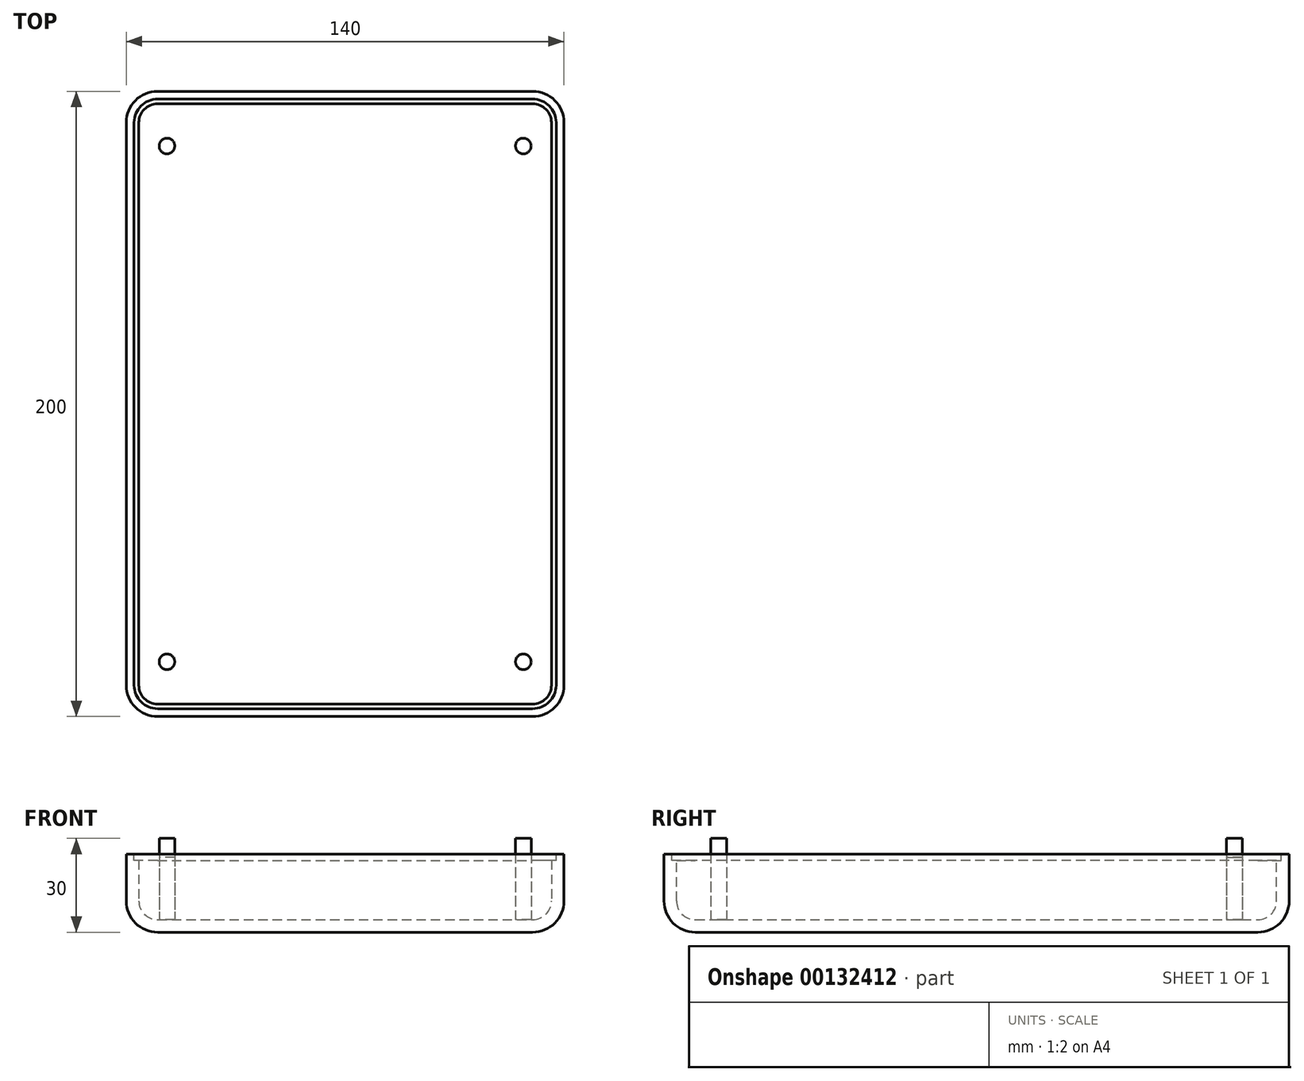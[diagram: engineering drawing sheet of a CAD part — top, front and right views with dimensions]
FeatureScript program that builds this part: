
annotation { "Feature Type Name" : "Feature", "Feature Type Description" : "" }
export const myFeature = defineFeature(function(context is Context, id is Id, definition is map)
    precondition{}
    {
        {
            var Q0;
            Q0=qCreatedBy(makeId("Top.planeOp"),FACE);
            var sketch = newSketch(context, id + "F0", { "sketchPlane" : qUnion([Q0])});
            skLineSegment(sketch, "E0.bottom", {"start": v(-140, 200) * mm, "end": v(0, 200) * mm});
            skLineSegment(sketch, "E0.top", {"start": v(-140, 0) * mm, "end": v(0, 0) * mm});
            skLineSegment(sketch, "E0.left", {"start": v(-140, 200) * mm, "end": v(-140, 0) * mm});
            skLineSegment(sketch, "E0.right", {"start": v(0, 200) * mm, "end": v(0, 0) * mm});
            skSolve(sketch);
        }
        {
            var Q0;
            Q0=makeQuery(id+"F0.imprint","IMPRINT",FACE,{"disambiguationData":[TD([[makeQuery(id+"F0.imprint","IMPRINT",EDGE,{"derivedFrom":sQuery(id+"F0.wireOp",EDGE,"E0.bottom")}),-1.0]])]});
            extrude(context, id + "F1", {"entities" : qUnion([Q0]), "depth" : 25 * mm});
        }
        {
            var Q0;
            Q0=makeQuery(id+"F1.opExtrude","CAP_EDGE",EDGE,{"disambiguationData":[OSD([sQuery(id+"F0.wireOp",EDGE,"E0.top")])],"isStart":true});
            var Q1;
            Q1=makeQuery(id+"F1.opExtrude","CAP_EDGE",EDGE,{"disambiguationData":[OSD([sQuery(id+"F0.wireOp",EDGE,"E0.left")])],"isStart":true});
            var Q2;
            Q2=makeQuery(id+"F1.opExtrude","CAP_EDGE",EDGE,{"disambiguationData":[OSD([sQuery(id+"F0.wireOp",EDGE,"E0.bottom")])],"isStart":true});
            var Q3;
            Q3=makeQuery(id+"F1.opExtrude","CAP_EDGE",EDGE,{"disambiguationData":[OSD([sQuery(id+"F0.wireOp",EDGE,"E0.right")])],"isStart":true});
            var Q4;
            Q4=makeQuery(id+"F1.opExtrude","SWEPT_EDGE",EDGE,{"disambiguationData":[OSD([sQuery(id+"F0.wireOp",EDGE,"E0.top"),sQuery(id+"F0.wireOp",EDGE,"E0.left")])]});
            var Q5;
            Q5=makeQuery(id+"F1.opExtrude","SWEPT_EDGE",EDGE,{"disambiguationData":[OSD([sQuery(id+"F0.wireOp",EDGE,"E0.top"),sQuery(id+"F0.wireOp",EDGE,"E0.right")])]});
            var Q6;
            Q6=makeQuery(id+"F1.opExtrude","SWEPT_EDGE",EDGE,{"disambiguationData":[OSD([sQuery(id+"F0.wireOp",EDGE,"E0.bottom"),sQuery(id+"F0.wireOp",EDGE,"E0.right")])]});
            var Q7;
            Q7=makeQuery(id+"F1.opExtrude","SWEPT_EDGE",EDGE,{"disambiguationData":[OSD([sQuery(id+"F0.wireOp",EDGE,"E0.bottom"),sQuery(id+"F0.wireOp",EDGE,"E0.left")])]});
            fillet(context, id + "F2", {"entities" : qUnion([Q0, Q1, Q2, Q3, Q4, Q5, Q6, Q7]), "radius" : 10 * mm, "tangentPropagation" : true, "allowEdgeOverflow" : false});
        }
        {
            var Q0;
            Q0=makeQuery(id+"F1.opExtrude","CAP_FACE",FACE,{"disambiguationData":[OSD([sQuery(id+"F0.wireOp",EDGE,"E0.bottom"),sQuery(id+"F0.wireOp",EDGE,"E0.top"),sQuery(id+"F0.wireOp",EDGE,"E0.left"),sQuery(id+"F0.wireOp",EDGE,"E0.right")])],"isStart":false});
            shell(context, id + "F3", {"entities" : qUnion([Q0]), "thickness" : 4 * mm});
        }
        {
            var Q0;
            Q0=makeQuery(id+"F1.opExtrude","CAP_FACE",FACE,{"disambiguationData":[OSD([sQuery(id+"F0.wireOp",EDGE,"E0.bottom"),sQuery(id+"F0.wireOp",EDGE,"E0.top"),sQuery(id+"F0.wireOp",EDGE,"E0.left"),sQuery(id+"F0.wireOp",EDGE,"E0.right")])],"isStart":false});
            var sketch = newSketch(context, id + "F4", { "sketchPlane" : qUnion([Q0])});
            skArc(sketch, "E1.0", {"start": v(-2.5, 190) * mm, "mid": v(-4.7, 195.3) * mm, "end": v(-10, 197.5) * mm});
            skLineSegment(sketch, "E1.1", {"start": v(-130, 197.5) * mm, "end": v(-10, 197.5) * mm});
            skLineSegment(sketch, "E1.2", {"start": v(-2.5, 190) * mm, "end": v(-2.5, 10) * mm});
            skArc(sketch, "E1.3", {"start": v(-130, 197.5) * mm, "mid": v(-135.3, 195.3) * mm, "end": v(-137.5, 190) * mm});
            skArc(sketch, "E1.4", {"start": v(-10, 2.5) * mm, "mid": v(-4.7, 4.7) * mm, "end": v(-2.5, 10) * mm});
            skLineSegment(sketch, "E1.5", {"start": v(-130, 2.5) * mm, "end": v(-10, 2.5) * mm});
            skArc(sketch, "E1.6", {"start": v(-137.5, 10) * mm, "mid": v(-135.3, 4.7) * mm, "end": v(-130, 2.5) * mm});
            skLineSegment(sketch, "E1.7", {"start": v(-137.5, 190) * mm, "end": v(-137.5, 10) * mm});
            skSolve(sketch);
        }
        {
            var Q0;
            Q0=makeQuery(id+"F4.imprint","IMPRINT",FACE,{"disambiguationData":[TD([[makeQuery(id+"F4.imprint","IMPRINT",EDGE,{"derivedFrom":sQuery(id+"F4.wireOp",EDGE,"E1.0")}),1.0]])]});
            extrude(context, id + "F5", {"entities" : qUnion([Q0]), "operationType" : NewBodyOperationType.REMOVE, "oppositeDirection" : true, "depth" : 2 * mm});
        }
        {
            var Q0;
            Q0=makeQuery(id+"F3.opShell","OFFSET_FACE",FACE,{"disambiguationData":[OSD([sQuery(id+"F0.wireOp",EDGE,"E0.bottom"),sQuery(id+"F0.wireOp",EDGE,"E0.top"),sQuery(id+"F0.wireOp",EDGE,"E0.left"),sQuery(id+"F0.wireOp",EDGE,"E0.right")])]});
            var sketch = newSketch(context, id + "F6", { "sketchPlane" : qUnion([Q0])});
            skLineSegment(sketch, "E2", {"start": v(-130, 190) * mm, "end": v(-10, 190) * mm, "construction": true});
            skLineSegment(sketch, "E3", {"start": v(-70, 190) * mm, "end": v(-70, -83.48) * mm, "construction": true});
            skPoint(sketch, "E3.endSnap0", {"position": v(-70, 10) * mm});
            skLineSegment(sketch, "E4.0", {"start": v(-13, 190) * mm, "end": v(-13, -93.48) * mm, "construction": true});
            skLineSegment(sketch, "E5.0", {"start": v(-5, 195) * mm, "end": v(-5, 5) * mm});
            skLineSegment(sketch, "E5.1", {"start": v(-5, 195) * mm, "end": v(-135, 195) * mm});
            skLineSegment(sketch, "E5.2", {"start": v(-135, 195) * mm, "end": v(-135, 5) * mm});
            skLineSegment(sketch, "E5.3", {"start": v(-5, 5) * mm, "end": v(-135, 5) * mm});
            skLineSegment(sketch, "E6.0", {"start": v(-127, 190) * mm, "end": v(-127, -93.48) * mm, "construction": true});
            skLineSegment(sketch, "E7", {"start": v(-127, 190) * mm, "end": v(-127, 10) * mm, "construction": true});
            skLineSegment(sketch, "E8", {"start": v(-127, 100) * mm, "end": v(14.67, 100) * mm, "construction": true});
            skLineSegment(sketch, "E9.0", {"start": v(-127, 17.5) * mm, "end": v(14.67, 17.5) * mm, "construction": true});
            skLineSegment(sketch, "E10.0", {"start": v(-127, 182.5) * mm, "end": v(14.67, 182.5) * mm, "construction": true});
            skCircle(sketch, "E11", {"center": v(-127, 182.5) * mm, "radius": 2.5 * mm});
            skCircle(sketch, "E12", {"center": v(-13, 182.5) * mm, "radius": 2.5 * mm});
            skCircle(sketch, "E13", {"center": v(-127, 17.5) * mm, "radius": 2.5 * mm});
            skCircle(sketch, "E14", {"center": v(-13, 17.5) * mm, "radius": 2.5 * mm});
            skSolve(sketch);
        }
        {
            var Q0;
            Q0=makeQuery(id+"F6.imprint","IMPRINT",FACE,{"disambiguationData":[TD([[makeQuery(id+"F6.imprint","IMPRINT",EDGE,{"derivedFrom":sQuery(id+"F6.wireOp",EDGE,"E11")}),1.0]])]});
            var Q1;
            Q1=makeQuery(id+"F6.imprint","IMPRINT",FACE,{"disambiguationData":[TD([[makeQuery(id+"F6.imprint","IMPRINT",EDGE,{"derivedFrom":sQuery(id+"F6.wireOp",EDGE,"E12")}),1.0]])]});
            var Q2;
            Q2=makeQuery(id+"F6.imprint","IMPRINT",FACE,{"disambiguationData":[TD([[makeQuery(id+"F6.imprint","IMPRINT",EDGE,{"derivedFrom":sQuery(id+"F6.wireOp",EDGE,"E13")}),1.0]])]});
            var Q3;
            Q3=makeQuery(id+"F6.imprint","IMPRINT",FACE,{"disambiguationData":[TD([[makeQuery(id+"F6.imprint","IMPRINT",EDGE,{"derivedFrom":sQuery(id+"F6.wireOp",EDGE,"E14")}),1.0]])]});
            extrude(context, id + "F7", {"entities" : qUnion([Q0, Q1, Q2, Q3]), "operationType" : NewBodyOperationType.ADD, "depth" : 26 * mm});
        }
        {
            var Q0;
            Q0=makeQuery(id+"F7.opExtrude","CAP_FACE",FACE,{"disambiguationData":[OSD([sQuery(id+"F6.wireOp",EDGE,"E11")])],"isStart":false});
            var sketch = newSketch(context, id + "F8", { "sketchPlane" : qUnion([Q0])});
            skCircle(sketch, "E15.0", {"center": v(-127, 182.5) * mm, "radius": 2.5 * mm});
            skSolve(sketch);
        }
        {
            var Q0;
            Q0 = qSketchRegion(id + "F8", true);
            extrude(context, id + "F9", {"entities" : qUnion([Q0]), "operationType" : NewBodyOperationType.REMOVE, "oppositeDirection" : true, "depth" : 6 * mm});
        }
        {
            var Q0;
            {var subQ0=sQuery(id+"F0.wireOp",EDGE,"E0.top");Q0=makeQuery(id+"F3.opShell","OFFSET_EDGE",EDGE,{"disambiguationData":[OSD([subQ0]),TDD([makeQuery(id+"F2.opFillet","BLEND_EDGE",EDGE,{"blendedFrom":[makeQuery(id+"F1.opExtrude","CAP_EDGE",EDGE,{"disambiguationData":[OSD([subQ0])],"isStart":true}),makeQuery(id+"F1.opExtrude","SWEPT_FACE",FACE,{"disambiguationData":[OSD([subQ0])]})],"blendedInto":[makeQuery(id+"F1.opExtrude","SWEPT_FACE",FACE,{"disambiguationData":[OSD([subQ0])]})]})])]});}
            cPoint(context, id + "F10", {"entities" : qUnion([Q0]), "parameter" : 0.5});
        }
        {
            var Q0;
            Q0=qCreatedBy(makeId("Right.planeOp"),FACE);
            var Q1;
            Q1 = qCreatedBy(id + "F10" ,VERTEX);
            cPlane(context, id + "F11", {"entities" : qUnion([Q0, Q1]), "cplaneType" : CPlaneType.PLANE_POINT, "offset" : 25 * mm, "width" : 150 * mm, "height" : 150 * mm});
        }
    });
